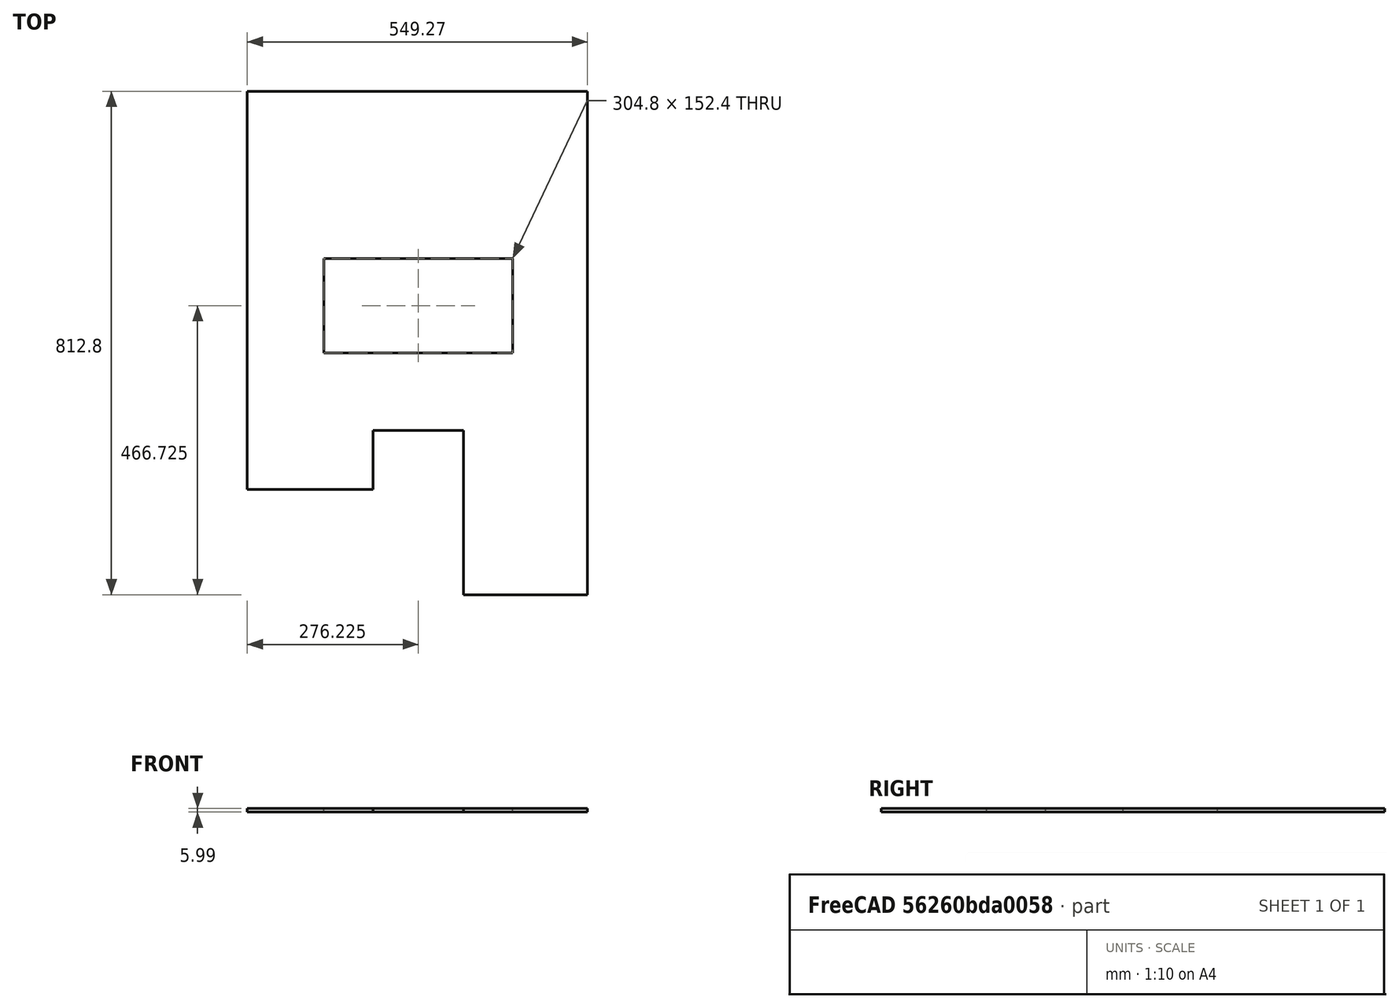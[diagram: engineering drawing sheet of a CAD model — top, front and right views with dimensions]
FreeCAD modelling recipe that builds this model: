
FCSTD DOCUMENT  (FreeCAD 0.19R24267 (Git))
Label: Inv2-P4
License: All rights reserved
LicenseURL: http://en.wikipedia.org/wiki/All_rights_reserved
objects: TechDraw::DrawViewDimension×12, TechDraw::DrawProjGroupItem×2, TechDraw::DrawHatch×2, TechDraw::DrawViewAnnotation×2, Sketcher::SketchObject×1, Part::Extrusion×1, TechDraw::DrawSVGTemplate×1, TechDraw::DrawProjGroup×1, TechDraw::DrawPage×1
note: 2 computed .brp shape members not serialized (recipe doc carries the construction recipe); baked Part::Feature solids carry a one-line shape summary decoded from their .brp

FEATURE [Sketcher::SketchObject] Sketch
  FullyConstrained = true
  sketch-geometry (12):
    g0: LineSegment StartX=0 StartY=-2.84e-14 StartZ=0 EndX=549.275 EndY=-2.84e-14 EndZ=0
    g1: LineSegment StartX=549.275 StartY=-2.84e-14 StartZ=0 EndX=549.275 EndY=-812.8 EndZ=0
    g2: LineSegment StartX=0 StartY=-2.84e-14 StartZ=0 EndX=0 EndY=-642.95 EndZ=0
    g3: LineSegment StartX=0 StartY=-642.95 StartZ=0 EndX=203.2 EndY=-642.95 EndZ=0
    g4: LineSegment StartX=549.275 StartY=-812.8 StartZ=0 EndX=349.25 EndY=-812.8 EndZ=0
    g5: LineSegment StartX=349.25 StartY=-812.8 StartZ=0 EndX=349.25 EndY=-547.675 EndZ=0
    g6: LineSegment StartX=349.25 StartY=-547.675 StartZ=0 EndX=203.2 EndY=-547.675 EndZ=0
    g7: LineSegment StartX=203.2 StartY=-547.675 StartZ=0 EndX=203.2 EndY=-642.95 EndZ=0
    g8: LineSegment StartX=123.825 StartY=-269.875 StartZ=0 EndX=428.625 EndY=-269.875 EndZ=0
    g9: LineSegment StartX=428.625 StartY=-269.875 StartZ=0 EndX=428.625 EndY=-422.275 EndZ=0
    g10: LineSegment StartX=428.625 StartY=-422.275 StartZ=0 EndX=123.825 EndY=-422.275 EndZ=0
    g11: LineSegment StartX=123.825 StartY=-422.275 StartZ=0 EndX=123.825 EndY=-269.875 EndZ=0
  constraints (35):
    c: Horizontal(g0)
    c: DistanceX(g0,g0) = 549.275
    c: Coincident(g1,g0)
    c: Vertical(g1)
    c: DistanceY(g1,g1) = 812.8
    c: Coincident(g2,g0)
    c: Vertical(g2)
    c: Coincident(g3,g2)
    c: Horizontal(g3)
    c: DistanceX(g3,g3) = 203.2
    c: Coincident(g4,g1)
    c: Horizontal(g4)
    c: DistanceX(g4,g4) = 200.025
    c: Coincident(g5,g4)
    c: Vertical(g5)
    c: DistanceY(g5,g5) = 265.125
    c: Coincident(g6,g5)
    c: Horizontal(g6)
    c: DistanceX(g6,g6) = 146.05
    c: Coincident(g7,g6)
    c: Coincident(g7,g3)
    c: Coincident(g8,g9)
    c: Coincident(g9,g10)
    c: Coincident(g10,g11)
    c: Coincident(g11,g8)
    c: Horizontal(g8)
    c: Horizontal(g10)
    c: Vertical(g9)
    c: Vertical(g11)
    c: DistanceX(g8,g8) = 304.8
    c: DistanceY(g11,g11) = 152.4
    c: DistanceX(g2,g10) = 123.825
    c: DistanceY(g1,g9) = 390.525
    c: Distance(g3,g4) = 169.85
    c: Coincident(g0,g-1)
FEATURE [Part::Extrusion] Extrude
  Base = -> Sketch
  Dir = (0,0,1)
  DirMode = 2
  FaceMakerClass = Part::FaceMakerBullseye
  LengthFwd = 5.9944
  LengthRev = 0
  Solid = true
  Symmetric = false
FEATURE [TechDraw::DrawSVGTemplate] Template
  Height = 215.9
  Orientation = 1
  Width = 279.4
FEATURE [TechDraw::DrawProjGroupItem] ProjItem  label="Front"
  CoarseView = false
  Direction = (0,0,1)
  Focus = 100
  HardHidden = false
  IsoCount = 0
  IsoHidden = false
  IsoVisible = false
  LockPosition = true
  Perspective = false
  Rotation = 0
  RotationVector = (1,0,0)
  Scale = 0.2
  ScaleType = 2
  SeamHidden = false
  SeamVisible = true
  SmoothHidden = false
  SmoothVisible = true
  Source = -> [Extrude]
  Type = 0
  X = 0
  XDirection = (1,0,0)
  Y = 0
FEATURE [TechDraw::DrawProjGroupItem] ProjItem001  label="Left"
  CoarseView = false
  Direction = (-1,0,1e-16)
  Focus = 100
  HardHidden = false
  IsoCount = 0
  IsoHidden = false
  IsoVisible = false
  LockPosition = false
  Perspective = false
  Rotation = 0
  RotationVector = (1,0,0)
  Scale = 0.2
  ScaleType = 2
  SeamHidden = false
  SeamVisible = true
  SmoothHidden = false
  SmoothVisible = true
  Source = -> [Extrude]
  Type = 1
  X = 90.2931
  XDirection = (1e-16,0,1)
  Y = 0
FEATURE [TechDraw::DrawProjGroup] ProjGroup
  Anchor = -> ProjItem
  AutoDistribute = true
  LockPosition = false
  ProjectionType = 0
  Rotation = 0
  Scale = 0.2
  ScaleType = 2
  Source = -> [Extrude]
  Views = -> [ProjItem,ProjItem001]
  X = 127.98
  Y = 110.757
  spacingX = 15.0114
  spacingY = 15.0114
FEATURE [TechDraw::DrawHatch] Hatch  label="HatchF0"
  HatchPattern = <path>
  Source = -> ProjItem [Face0]
FEATURE [TechDraw::DrawHatch] Hatch001  label="Hatch001F2"
  HatchPattern = <path>
  Source = -> ProjItem001 [Face2,Face1]
FEATURE [TechDraw::DrawViewDimension] Dimension
  Arbitrary = false
  ArbitraryTolerances = false
  EqualTolerance = true
  FormatSpec = %.3f
  FormatSpecOverTolerance = %+.3f
  FormatSpecUnderTolerance = %+.3f
  Inverted = false
  LockPosition = false
  MeasureType = 1
  OverTolerance = 0
  References2D = -> [ProjItem]
  Rotation = 0
  ScaleType = 0
  TheoreticalExact = false
  Type = 2
  UnderTolerance = 0
  X = 65.0174
  Y = 1.68165
FEATURE [TechDraw::DrawViewDimension] Dimension001
  Arbitrary = false
  ArbitraryTolerances = false
  EqualTolerance = true
  FormatSpec = %.3f
  FormatSpecOverTolerance = %+.3f
  FormatSpecUnderTolerance = %+.3f
  Inverted = false
  LockPosition = false
  MeasureType = 1
  OverTolerance = 0
  References2D = -> [ProjItem001]
  Rotation = 0
  ScaleType = 0
  TheoreticalExact = false
  Type = 1
  UnderTolerance = 0
  X = 12.9131
  Y = 77.3544
FEATURE [TechDraw::DrawViewDimension] Dimension002
  Arbitrary = false
  ArbitraryTolerances = false
  EqualTolerance = true
  FormatSpec = %.3f
  FormatSpecOverTolerance = %+.3f
  FormatSpecUnderTolerance = %+.3f
  Inverted = false
  LockPosition = false
  MeasureType = 1
  OverTolerance = 0
  References2D = -> [ProjItem]
  Rotation = 0
  ScaleType = 0
  TheoreticalExact = false
  Type = 1
  UnderTolerance = 0
  X = 0.73686
  Y = 95.6488
FEATURE [TechDraw::DrawViewDimension] Dimension003
  Arbitrary = false
  ArbitraryTolerances = false
  EqualTolerance = true
  FormatSpec = %.3f
  FormatSpecOverTolerance = %+.3f
  FormatSpecUnderTolerance = %+.3f
  Inverted = false
  LockPosition = false
  MeasureType = 1
  OverTolerance = 0
  References2D = -> [ProjItem]
  Rotation = 0
  ScaleType = 0
  TheoreticalExact = false
  Type = 1
  UnderTolerance = 0
  X = -2.62994
  Y = -51.8345
FEATURE [TechDraw::DrawViewDimension] Dimension004
  Arbitrary = false
  ArbitraryTolerances = false
  EqualTolerance = true
  FormatSpec = %.3f
  FormatSpecOverTolerance = %+.3f
  FormatSpecUnderTolerance = %+.3f
  Inverted = false
  LockPosition = false
  MeasureType = 1
  OverTolerance = 0
  References2D = -> [ProjItem]
  Rotation = 0
  ScaleType = 0
  TheoreticalExact = false
  Type = 1
  UnderTolerance = 0
  X = -35.7128
  Y = -51.7312
FEATURE [TechDraw::DrawViewDimension] Dimension005
  Arbitrary = false
  ArbitraryTolerances = false
  EqualTolerance = true
  FormatSpec = %.3f
  FormatSpecOverTolerance = %+.3f
  FormatSpecUnderTolerance = %+.3f
  Inverted = false
  LockPosition = false
  MeasureType = 1
  OverTolerance = 0
  References2D = -> [ProjItem]
  Rotation = 0
  ScaleType = 0
  TheoreticalExact = false
  Type = 2
  UnderTolerance = 0
  X = -80.7371
  Y = -63.5582
FEATURE [TechDraw::DrawViewDimension] Dimension006
  Arbitrary = false
  ArbitraryTolerances = false
  EqualTolerance = true
  FormatSpec = %.3f
  FormatSpecOverTolerance = %+.3f
  FormatSpecUnderTolerance = %+.3f
  Inverted = false
  LockPosition = false
  MeasureType = 1
  OverTolerance = 0
  References2D = -> [ProjItem]
  Rotation = 0
  ScaleType = 0
  TheoreticalExact = false
  Type = 2
  UnderTolerance = 0
  X = 35.5546
  Y = -54.3991
FEATURE [TechDraw::DrawViewDimension] Dimension007
  Arbitrary = false
  ArbitraryTolerances = false
  EqualTolerance = true
  FormatSpec = %.3f
  FormatSpecOverTolerance = %+.3f
  FormatSpecUnderTolerance = %+.3f
  Inverted = false
  LockPosition = false
  MeasureType = 1
  OverTolerance = 0
  References2D = -> [ProjItem]
  Rotation = 0
  ScaleType = 0
  TheoreticalExact = false
  Type = 1
  UnderTolerance = 0
  X = -0.018829
  Y = -6.66423
FEATURE [TechDraw::DrawViewDimension] Dimension008
  Arbitrary = false
  ArbitraryTolerances = false
  EqualTolerance = true
  FormatSpec = %.3f
  FormatSpecOverTolerance = %+.3f
  FormatSpecUnderTolerance = %+.3f
  Inverted = false
  LockPosition = false
  MeasureType = 1
  OverTolerance = 0
  References2D = -> [ProjItem]
  Rotation = 0
  ScaleType = 0
  TheoreticalExact = false
  Type = 2
  UnderTolerance = 0
  X = -40.925
  Y = 14.4193
FEATURE [TechDraw::DrawViewDimension] Dimension009
  Arbitrary = false
  ArbitraryTolerances = false
  EqualTolerance = true
  FormatSpec = %.3f
  FormatSpecOverTolerance = %+.3f
  FormatSpecUnderTolerance = %+.3f
  Inverted = false
  LockPosition = false
  MeasureType = 1
  OverTolerance = 0
  References2D = -> [ProjItem]
  Rotation = 0
  ScaleType = 0
  TheoreticalExact = false
  Type = 1
  UnderTolerance = 0
  X = 45.3107
  Y = -6.62511
FEATURE [TechDraw::DrawViewDimension] Dimension010
  Arbitrary = false
  ArbitraryTolerances = false
  EqualTolerance = true
  FormatSpec = %.3f
  FormatSpecOverTolerance = %+.3f
  FormatSpecUnderTolerance = %+.3f
  Inverted = false
  LockPosition = false
  MeasureType = 1
  OverTolerance = 0
  References2D = -> [ProjItem]
  Rotation = 0
  ScaleType = 0
  TheoreticalExact = false
  Type = 2
  UnderTolerance = 0
  X = -40.8458
  Y = 54.2925
FEATURE [TechDraw::DrawViewAnnotation] Annotation
  Font = osifont
  LineSpace = 80
  LockPosition = false
  MaxWidth = -1
  Rotation = 0
  ScaleType = 0
  Text = Figure S2 (Inverted 2) | Panel 4 [front] | Quantity: 1
  TextSize = 5.0038
  TextStyle = 0
  X = 32.643
  Y = 195.58
FEATURE [TechDraw::DrawViewAnnotation] Annotation002
  Font = osifont
  LineSpace = 80
  LockPosition = false
  MaxWidth = -1
  Rotation = 0
  ScaleType = 0
  Text = Units: Inches
  TextSize = 5.0038
  TextStyle = 0
  X = 259.08
  Y = 5.08
FEATURE [TechDraw::DrawViewDimension] Dimension011
  Arbitrary = false
  ArbitraryTolerances = false
  EqualTolerance = true
  FormatSpec = %.3f
  FormatSpecOverTolerance = %+.3f
  FormatSpecUnderTolerance = %+.3f
  Inverted = false
  LockPosition = false
  MeasureType = 1
  OverTolerance = 0
  References2D = -> [ProjItem]
  Rotation = 0
  ScaleType = 0
  TheoreticalExact = false
  Type = 1
  UnderTolerance = 0
  X = 34.2523
  Y = -88.3429
FEATURE [TechDraw::DrawPage] Page
  KeepUpdated = true
  NextBalloonIndex = 1
  ProjectionType = 0
  Template = -> Template
  Views = -> [ProjGroup,Dimension,Dimension001,Dimension002,Dimension003,Dimension004,Dimension005,Dimension006,Dimension007,Dimension008,Dimension009,Dimension010,Annotation,Annotation002,Dimension011]
note: 2 file-system paths scrubbed to <path> (originals preserved in the JSON sidecar)
